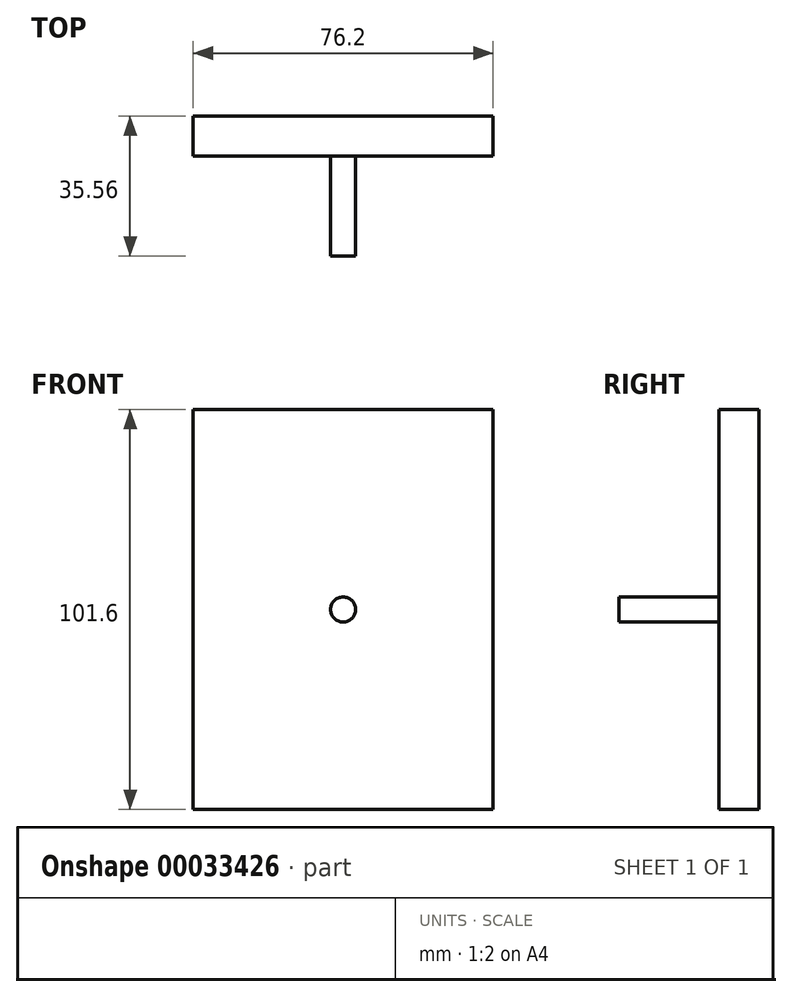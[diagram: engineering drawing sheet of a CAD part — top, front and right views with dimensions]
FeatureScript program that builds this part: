
annotation { "Feature Type Name" : "Feature", "Feature Type Description" : "" }
export const myFeature = defineFeature(function(context is Context, id is Id, definition is map)
    precondition{}
    {
        {
            var Q0;
            Q0=qCreatedBy(makeId("Front.planeOp"),FACE);
            var sketch = newSketch(context, id + "F0", { "sketchPlane" : qUnion([Q0])});
            skLineSegment(sketch, "E0.rect.bottom", {"start": v(-38.1, 50.8) * mm, "end": v(38.1, 50.8) * mm});
            skLineSegment(sketch, "E0.rect.top", {"start": v(-38.1, -50.8) * mm, "end": v(38.1, -50.8) * mm});
            skLineSegment(sketch, "E0.rect.left", {"start": v(-38.1, 50.8) * mm, "end": v(-38.1, -50.8) * mm});
            skLineSegment(sketch, "E0.rect.right", {"start": v(38.1, 50.8) * mm, "end": v(38.1, -50.8) * mm});
            skPoint(sketch, "E0.rect.middle", {"position": v(0, 0) * mm});
            skCircle(sketch, "E1", {"center": v(0, 0) * mm, "radius": 3.18 * mm});
            skSolve(sketch);
        }
        {
            var Q0;
            Q0=makeQuery(id+"F0.imprint","IMPRINT",FACE,{"disambiguationData":[TD([[makeQuery(id+"F0.imprint","IMPRINT",EDGE,{"derivedFrom":sQuery(id+"F0.wireOp",EDGE,"E1")}),1.0]])]});
            extrude(context, id + "F1", {"entities" : qUnion([Q0]), "depth" : 35.56 * mm});
        }
        {
            var Q0;
            Q0 = qSketchRegion(id + "F0", true);
            extrude(context, id + "F2", {"entities" : qUnion([Q0]), "operationType" : NewBodyOperationType.ADD, "depth" : 10.16 * mm});
        }
    });
